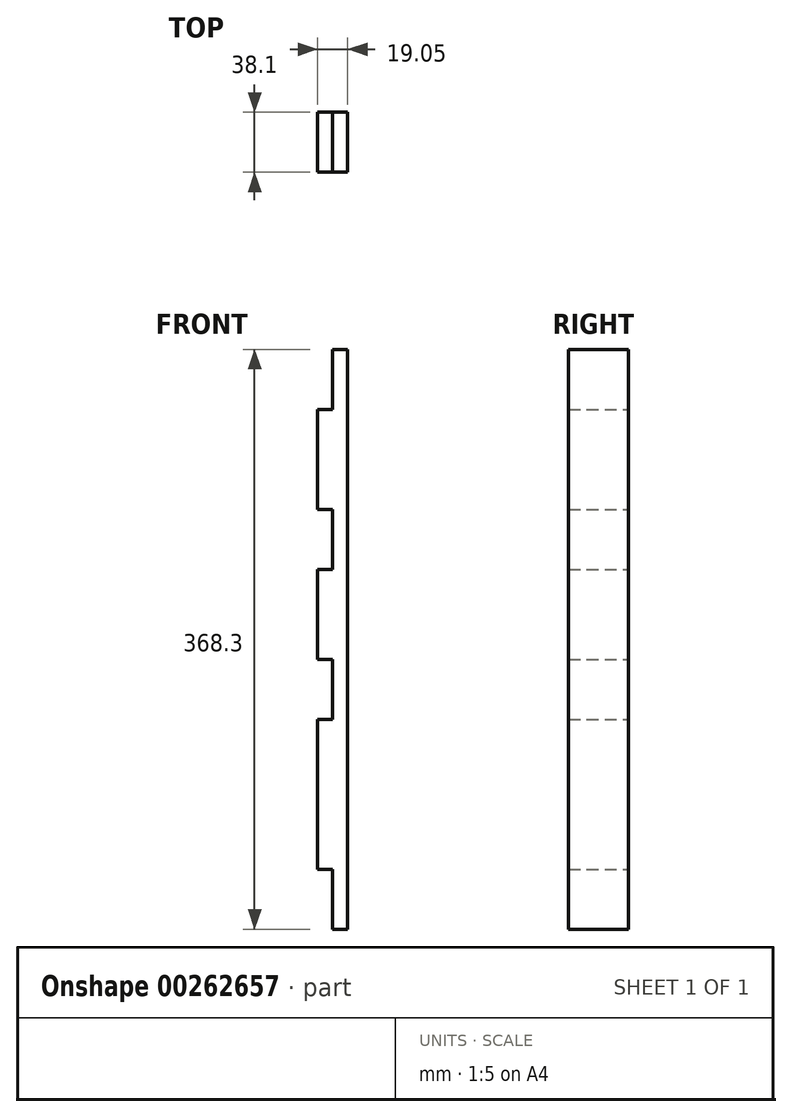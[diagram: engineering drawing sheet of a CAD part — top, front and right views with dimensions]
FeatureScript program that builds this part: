
annotation { "Feature Type Name" : "Feature", "Feature Type Description" : "" }
export const myFeature = defineFeature(function(context is Context, id is Id, definition is map)
    precondition{}
    {
        {
            var Q0;
            Q0=qCreatedBy(makeId("Front.planeOp"),FACE);
            var sketch = newSketch(context, id + "F0", { "sketchPlane" : qUnion([Q0])});
            skLineSegment(sketch, "E0", {"start": v(0, 0) * mm, "end": v(0, -368.3) * mm});
            skLineSegment(sketch, "E1", {"start": v(0, 0) * mm, "end": v(-9.53, 0) * mm});
            skLineSegment(sketch, "E2", {"start": v(-9.53, 0) * mm, "end": v(-9.53, -38.1) * mm});
            skLineSegment(sketch, "E3", {"start": v(-9.52, -38.1) * mm, "end": v(-19.05, -38.1) * mm});
            skLineSegment(sketch, "E4", {"start": v(-19.05, -38.1) * mm, "end": v(-19.05, -101.6) * mm});
            skLineSegment(sketch, "E5", {"start": v(-19.05, -101.6) * mm, "end": v(-9.52, -101.6) * mm});
            skLineSegment(sketch, "E6", {"start": v(-9.53, -101.6) * mm, "end": v(-9.52, -139.7) * mm});
            skLineSegment(sketch, "E7", {"start": v(-9.52, -139.7) * mm, "end": v(-19.05, -139.7) * mm});
            skLineSegment(sketch, "E8", {"start": v(-19.05, -139.7) * mm, "end": v(-19.05, -196.85) * mm});
            skLineSegment(sketch, "E9", {"start": v(-19.05, -196.85) * mm, "end": v(-9.52, -196.85) * mm});
            skLineSegment(sketch, "E10", {"start": v(-9.53, -196.85) * mm, "end": v(-9.53, -234.95) * mm});
            skLineSegment(sketch, "E11", {"start": v(-9.52, -234.95) * mm, "end": v(-19.05, -234.95) * mm});
            skLineSegment(sketch, "E12", {"start": v(-19.05, -234.95) * mm, "end": v(-19.05, -330.2) * mm});
            skLineSegment(sketch, "E13", {"start": v(-19.05, -330.2) * mm, "end": v(-9.52, -330.2) * mm});
            skLineSegment(sketch, "E14", {"start": v(-9.53, -330.2) * mm, "end": v(-9.52, -368.3) * mm});
            skLineSegment(sketch, "E15", {"start": v(-9.53, -368.3) * mm, "end": v(0, -368.3) * mm});
            skSolve(sketch);
        }
        {
            var Q0;
            Q0=makeQuery(id+"F0.imprint","IMPRINT",FACE,{"disambiguationData":[TD([[makeQuery(id+"F0.imprint","IMPRINT",EDGE,{"derivedFrom":sQuery(id+"F0.wireOp",EDGE,"E0")}),-1.0]])]});
            extrude(context, id + "F1", {"entities" : qUnion([Q0]), "depth" : 38.1 * mm});
        }
    });
